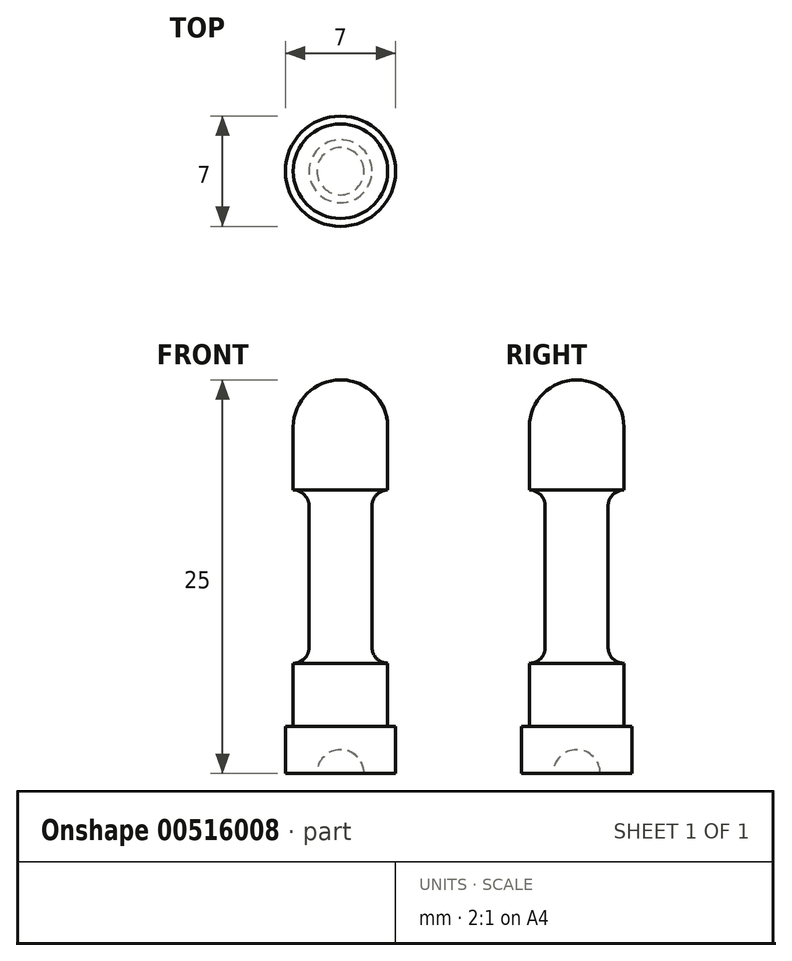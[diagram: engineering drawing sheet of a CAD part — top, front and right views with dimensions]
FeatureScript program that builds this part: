
annotation { "Feature Type Name" : "Feature", "Feature Type Description" : "" }
export const myFeature = defineFeature(function(context is Context, id is Id, definition is map)
    precondition{}
    {
        {
            var Q0;
            Q0=qCreatedBy(makeId("Front.planeOp"),FACE);
            var sketch = newSketch(context, id + "F0", { "sketchPlane" : qUnion([Q0])});
            skArc(sketch, "E0", {"start": v(1.5, 0) * mm, "mid": v(1.06, 1.06) * mm, "end": v(0, 1.5) * mm});
            skLineSegment(sketch, "E1", {"start": v(0, 1.5) * mm, "end": v(0, 25) * mm, "construction": true});
            skLineSegment(sketch, "E2.bottom", {"start": v(1.5, 0) * mm, "end": v(3.5, 0) * mm});
            skLineSegment(sketch, "E2.top", {"start": v(3, 3) * mm, "end": v(3.5, 3) * mm});
            skLineSegment(sketch, "E2.left", {"start": v(0, 0) * mm, "end": v(0, 3) * mm});
            skLineSegment(sketch, "E2.right", {"start": v(3.5, 0) * mm, "end": v(3.5, 3) * mm});
            skLineSegment(sketch, "E3", {"start": v(3, 3) * mm, "end": v(3, 7) * mm});
            skLineSegment(sketch, "E4", {"start": v(2, 7) * mm, "end": v(3, 7) * mm});
            skLineSegment(sketch, "E5", {"start": v(2, 7) * mm, "end": v(2, 18) * mm});
            skLineSegment(sketch, "E6", {"start": v(2, 18) * mm, "end": v(3, 18) * mm});
            skLineSegment(sketch, "E7", {"start": v(3, 18) * mm, "end": v(3, 22) * mm});
            skLineSegment(sketch, "E8", {"start": v(3, 22) * mm, "end": v(0, 22) * mm});
            skPoint(sketch, "E9.orphan", {"position": v(0, 7) * mm});
            skPoint(sketch, "E10.start.orphan", {"position": v(0, 18) * mm});
            skArc(sketch, "E11", {"start": v(3, 22) * mm, "mid": v(2.12, 24.12) * mm, "end": v(0, 25) * mm});
            skLineSegment(sketch, "E12", {"start": v(0, 25) * mm, "end": v(0, 1.5) * mm});
            skSolve(sketch);
        }
        {
            var Q0;
            {var subQ0=sQuery(id+"F0.wireOp",EDGE,"E8");Q0=makeQuery(id+"F0.imprint","IMPRINT",FACE,{"disambiguationData":[TD([[makeQuery(id+"F0.imprint","IMPRINT",EDGE,{"derivedFrom":subQ0}),-1.0]])]});}
            var Q1;
            {var subQ1=sQuery(id+"F0.wireOp",EDGE,"E0");Q1=makeQuery(id+"F0.imprint","IMPRINT",FACE,{"disambiguationData":[TD([[makeQuery(id+"F0.imprint","IMPRINT",EDGE,{"derivedFrom":subQ1}),-1.0]])]});}
            var Q2;
            Q2=sQuery(id+"F0.wireOp",EDGE,"E12");
            revolve(context, id + "F1", {"entities" : qUnion([Q0, Q1]), "axis" : qUnion([Q2]), "revolveType" : RevolveType.FULL});
        }
        {
            var Q0;
            Q0=makeQuery(id+"F1.opRevolve","SWEPT_EDGE",EDGE,{"disambiguationData":[OSD([sQuery(id+"F0.wireOp",EDGE,"E5"),sQuery(id+"F0.wireOp",EDGE,"E6")])]});
            var Q1;
            Q1=makeQuery(id+"F1.opRevolve","SWEPT_EDGE",EDGE,{"disambiguationData":[OSD([sQuery(id+"F0.wireOp",EDGE,"E4"),sQuery(id+"F0.wireOp",EDGE,"E5")])]});
            fillet(context, id + "F2", {"entities" : qUnion([Q0, Q1]), "radius" : 1 * mm, "tangentPropagation" : true, "allowEdgeOverflow" : false});
        }
    });
